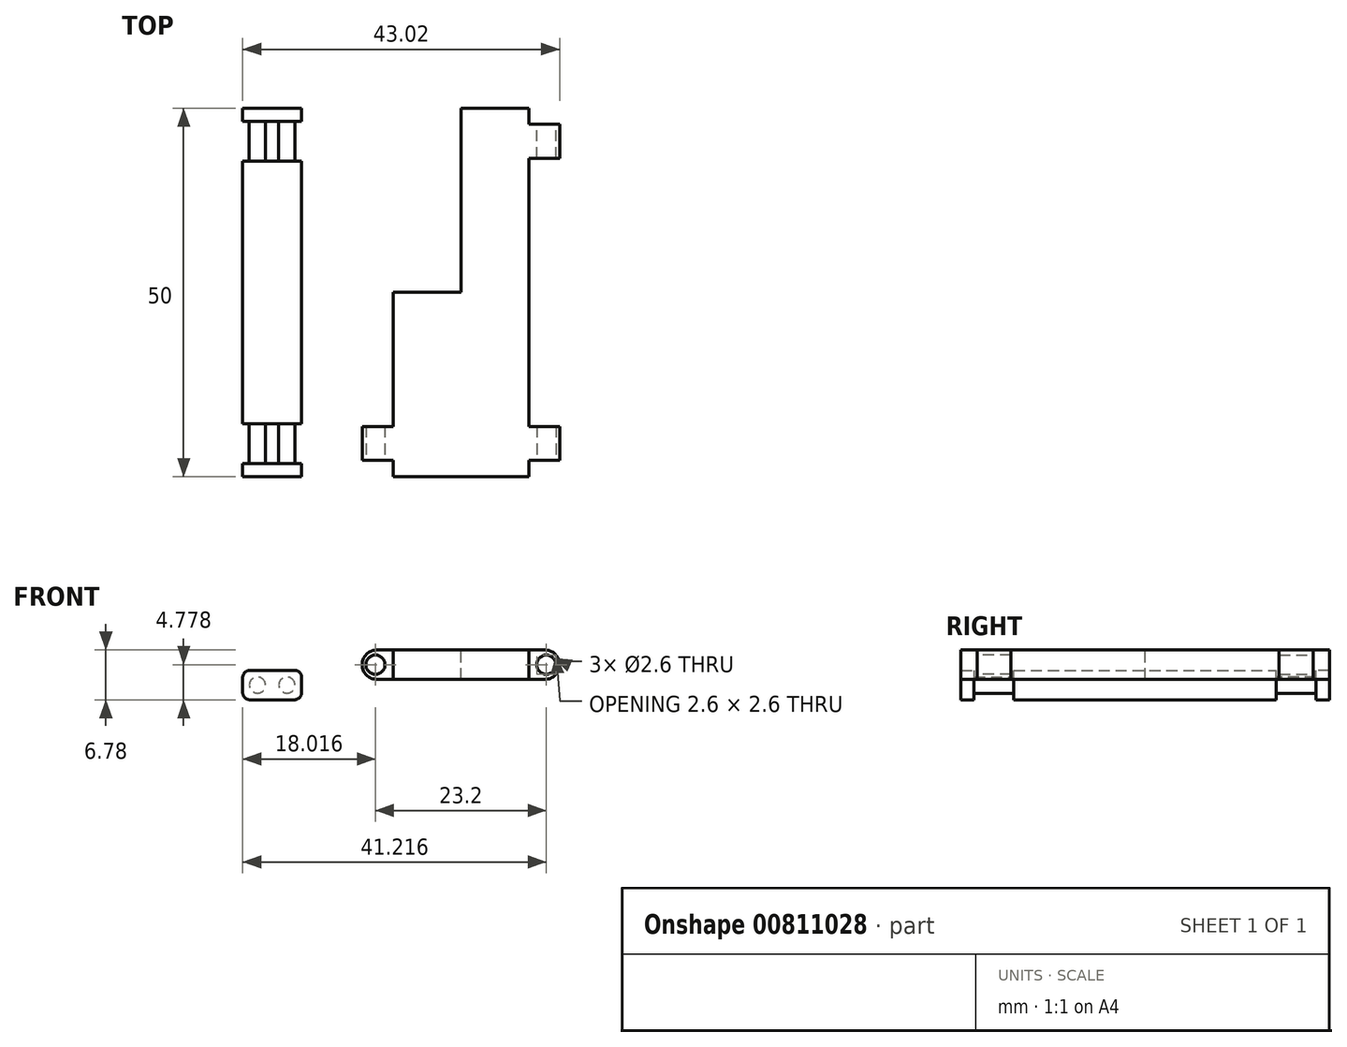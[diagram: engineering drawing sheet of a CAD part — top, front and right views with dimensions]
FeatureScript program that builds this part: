
annotation { "Feature Type Name" : "Feature", "Feature Type Description" : "" }
export const myFeature = defineFeature(function(context is Context, id is Id, definition is map)
    precondition{}
    {
        {
            var Q0;
            Q0=qCreatedBy(makeId("Front.planeOp"),FACE);
            var sketch = newSketch(context, id + "F0", { "sketchPlane" : qUnion([Q0])});
            skLineSegment(sketch, "E0.bottom", {"start": v(-56.99, 28.8) * mm, "end": v(-48.99, 28.8) * mm});
            skLineSegment(sketch, "E0.top", {"start": v(-56.99, 24.8) * mm, "end": v(-48.99, 24.8) * mm});
            skLineSegment(sketch, "E0.left", {"start": v(-56.99, 28.8) * mm, "end": v(-56.99, 24.8) * mm});
            skLineSegment(sketch, "E0.right", {"start": v(-48.99, 28.8) * mm, "end": v(-48.99, 24.8) * mm});
            skSolve(sketch);
        }
        {
            var Q0;
            Q0 = qSketchRegion(id + "F0", true);
            extrude(context, id + "F1", {"entities" : qUnion([Q0]), "depth" : 25 * mm, "offsetDistance" : 25 * mm});
        }
        {
            var Q0;
            Q0=makeQuery(id+"F1.opExtrude","SWEPT_FACE",FACE,{"disambiguationData":[OSD([sQuery(id+"F0.wireOp",EDGE,"E0.bottom")])]});
            var sketch = newSketch(context, id + "F2", { "sketchPlane" : qUnion([Q0])});
            skLineSegment(sketch, "E1.bottom", {"start": v(-56.99, -23.2) * mm, "end": v(-48.99, -23.2) * mm});
            skLineSegment(sketch, "E1.top", {"start": v(-56.99, -17.8) * mm, "end": v(-48.99, -17.8) * mm});
            skLineSegment(sketch, "E1.left", {"start": v(-56.99, -23.2) * mm, "end": v(-56.99, -17.8) * mm});
            skLineSegment(sketch, "E1.right", {"start": v(-48.99, -23.2) * mm, "end": v(-48.99, -17.8) * mm});
            skSolve(sketch);
        }
        {
            var Q0;
            Q0 = qSketchRegion(id + "F2", true);
            extrude(context, id + "F3", {"entities" : qUnion([Q0]), "operationType" : NewBodyOperationType.REMOVE, "oppositeDirection" : true, "depth" : 25 * mm, "offsetDistance" : 25 * mm});
        }
        {
            var Q0;
            Q0=makeQuery(id+"F3.boolean.opBoolean","COPY",FACE,{"derivedFrom":makeQuery(id+"F3.opExtrude","SWEPT_FACE",FACE,{"disambiguationData":[OSD([sQuery(id+"F2.wireOp",EDGE,"E1.top")])]})});
            var sketch = newSketch(context, id + "F4", { "sketchPlane" : qUnion([Q0])});
            skCircle(sketch, "E2", {"center": v(-54.99, 26.8) * mm, "radius": 1.1 * mm});
            skCircle(sketch, "E3", {"center": v(-50.99, 26.8) * mm, "radius": 1.1 * mm});
            skLineSegment(sketch, "E4", {"start": v(-56.99, 26.8) * mm, "end": v(-48.99, 26.8) * mm, "construction": true});
            skSolve(sketch);
        }
        {
            var Q0;
            Q0 = qSketchRegion(id + "F4", true);
            extrude(context, id + "F5", {"entities" : qUnion([Q0]), "operationType" : NewBodyOperationType.ADD, "depth" : 7 * mm, "offsetDistance" : 25 * mm});
        }
        {
            var Q0;
            {var subQ0=sQuery(id+"F0.wireOp",EDGE,"E0.bottom");var subQ1=sQuery(id+"F0.wireOp",EDGE,"E0.left");Q0=makeQuery(id+"F3.boolean.opBoolean","SPLIT",EDGE,{"disambiguationData":[TD([makeQuery(id+"F3.opExtrude","SWEPT_FACE",FACE,{"disambiguationData":[OSD([sQuery(id+"F2.wireOp",EDGE,"E1.top")])]})])],"derivedFrom":makeQuery(id+"F1.opExtrude","SWEPT_EDGE",EDGE,{"disambiguationData":[OSD([subQ0,subQ1])]})});}
            var Q1;
            {var subQ0=sQuery(id+"F0.wireOp",EDGE,"E0.bottom");var subQ1=sQuery(id+"F0.wireOp",EDGE,"E0.right");Q1=makeQuery(id+"F3.boolean.opBoolean","SPLIT",EDGE,{"disambiguationData":[TD([makeQuery(id+"F3.opExtrude","SWEPT_FACE",FACE,{"disambiguationData":[OSD([sQuery(id+"F2.wireOp",EDGE,"E1.top")])]})])],"derivedFrom":makeQuery(id+"F1.opExtrude","SWEPT_EDGE",EDGE,{"disambiguationData":[OSD([subQ0,subQ1])]})});}
            var Q2;
            {var subQ0=sQuery(id+"F0.wireOp",EDGE,"E0.right");var subQ1=sQuery(id+"F0.wireOp",EDGE,"E0.top");Q2=makeQuery(id+"F3.boolean.opBoolean","SPLIT",EDGE,{"disambiguationData":[TD([makeQuery(id+"F3.opExtrude","SWEPT_FACE",FACE,{"disambiguationData":[OSD([sQuery(id+"F2.wireOp",EDGE,"E1.top")])]})])],"derivedFrom":makeQuery(id+"F1.opExtrude","SWEPT_EDGE",EDGE,{"disambiguationData":[OSD([subQ1,subQ0])]})});}
            var Q3;
            {var subQ0=sQuery(id+"F0.wireOp",EDGE,"E0.bottom");var subQ1=sQuery(id+"F0.wireOp",EDGE,"E0.right");Q3=makeQuery(id+"F3.boolean.opBoolean","SPLIT",EDGE,{"disambiguationData":[TD([makeQuery(id+"F3.opExtrude","SWEPT_FACE",FACE,{"disambiguationData":[OSD([sQuery(id+"F2.wireOp",EDGE,"E1.bottom")])]})])],"derivedFrom":makeQuery(id+"F1.opExtrude","SWEPT_EDGE",EDGE,{"disambiguationData":[OSD([subQ0,subQ1])]})});}
            var Q4;
            {var subQ0=sQuery(id+"F0.wireOp",EDGE,"E0.bottom");var subQ1=sQuery(id+"F0.wireOp",EDGE,"E0.left");Q4=makeQuery(id+"F3.boolean.opBoolean","SPLIT",EDGE,{"disambiguationData":[TD([makeQuery(id+"F3.opExtrude","SWEPT_FACE",FACE,{"disambiguationData":[OSD([sQuery(id+"F2.wireOp",EDGE,"E1.bottom")])]})])],"derivedFrom":makeQuery(id+"F1.opExtrude","SWEPT_EDGE",EDGE,{"disambiguationData":[OSD([subQ0,subQ1])]})});}
            var Q5;
            {var subQ0=sQuery(id+"F0.wireOp",EDGE,"E0.right");var subQ1=sQuery(id+"F0.wireOp",EDGE,"E0.top");Q5=makeQuery(id+"F3.boolean.opBoolean","SPLIT",EDGE,{"disambiguationData":[TD([makeQuery(id+"F3.opExtrude","SWEPT_FACE",FACE,{"disambiguationData":[OSD([sQuery(id+"F2.wireOp",EDGE,"E1.bottom")])]})])],"derivedFrom":makeQuery(id+"F1.opExtrude","SWEPT_EDGE",EDGE,{"disambiguationData":[OSD([subQ1,subQ0])]})});}
            var Q6;
            {var subQ0=sQuery(id+"F0.wireOp",EDGE,"E0.left");var subQ1=sQuery(id+"F0.wireOp",EDGE,"E0.top");Q6=makeQuery(id+"F3.boolean.opBoolean","SPLIT",EDGE,{"disambiguationData":[TD([makeQuery(id+"F3.opExtrude","SWEPT_FACE",FACE,{"disambiguationData":[OSD([sQuery(id+"F2.wireOp",EDGE,"E1.top")])]})])],"derivedFrom":makeQuery(id+"F1.opExtrude","SWEPT_EDGE",EDGE,{"disambiguationData":[OSD([subQ1,subQ0])]})});}
            var Q7;
            {var subQ0=sQuery(id+"F0.wireOp",EDGE,"E0.left");var subQ1=sQuery(id+"F0.wireOp",EDGE,"E0.top");Q7=makeQuery(id+"F3.boolean.opBoolean","SPLIT",EDGE,{"disambiguationData":[TD([makeQuery(id+"F3.opExtrude","SWEPT_FACE",FACE,{"disambiguationData":[OSD([sQuery(id+"F2.wireOp",EDGE,"E1.bottom")])]})])],"derivedFrom":makeQuery(id+"F1.opExtrude","SWEPT_EDGE",EDGE,{"disambiguationData":[OSD([subQ1,subQ0])]})});}
            fillet(context, id + "F6", {"entities" : qUnion([Q0, Q1, Q2, Q3, Q4, Q5, Q6, Q7]), "radius" : 1 * mm, "tangentPropagation" : true, "allowEdgeOverflow" : false});
        }
        {
            var Q0;
            Q0=makeQuery(id+"F3.boolean.opBoolean","SPLIT",BODY,{"disambiguationData":[OD(0.0)],"derivedFrom":makeQuery(id+"F1.opExtrude","SWEPT_BODY",BODY,{"disambiguationData":[OSD([sQuery(id+"F0.wireOp",EDGE,"E0.bottom"),sQuery(id+"F0.wireOp",EDGE,"E0.top"),sQuery(id+"F0.wireOp",EDGE,"E0.left"),sQuery(id+"F0.wireOp",EDGE,"E0.right")])]})});
            var Q1;
            Q1=qCreatedBy(makeId("Front.planeOp"),FACE);
            mirror(context, id + "F7", {"operationType" : NewBodyOperationType.ADD, "entities" : qUnion([Q0]), "mirrorPlane" : qUnion([Q1])});
        }
        {
            var Q0;
            Q0=qCreatedBy(makeId("Front.planeOp"),FACE);
            var sketch = newSketch(context, id + "F8", { "sketchPlane" : qUnion([Q0])});
            skLineSegment(sketch, "E5.bottom", {"start": v(-27.37, 27.57) * mm, "end": v(-18.17, 27.57) * mm});
            skLineSegment(sketch, "E5.top", {"start": v(-27.37, 31.57) * mm, "end": v(-18.17, 31.57) * mm});
            skLineSegment(sketch, "E5.left", {"start": v(-27.37, 27.57) * mm, "end": v(-27.37, 31.57) * mm});
            skLineSegment(sketch, "E5.right", {"start": v(-18.17, 27.57) * mm, "end": v(-18.17, 31.57) * mm});
            skSolve(sketch);
        }
        {
            var Q0;
            Q0 = qSketchRegion(id + "F8", true);
            extrude(context, id + "F9", {"entities" : qUnion([Q0]), "depth" : 25 * mm, "offsetDistance" : 25 * mm});
        }
        {
            var Q0;
            Q0=makeQuery(id+"F9.opExtrude","SWEPT_FACE",FACE,{"disambiguationData":[OSD([sQuery(id+"F8.wireOp",EDGE,"E5.right")])]});
            var sketch = newSketch(context, id + "F10", { "sketchPlane" : qUnion([Q0])});
            skLineSegment(sketch, "E6", {"start": v(-23, 31.57) * mm, "end": v(-23, 27.57) * mm, "construction": true});
            skLineSegment(sketch, "E7", {"start": v(-18, 31.57) * mm, "end": v(-18, 27.57) * mm, "construction": true});
            skLineSegment(sketch, "E8.bottom", {"start": v(-22.8, 31.57) * mm, "end": v(-18.2, 31.57) * mm});
            skLineSegment(sketch, "E8.top", {"start": v(-22.8, 27.57) * mm, "end": v(-18.2, 27.57) * mm});
            skLineSegment(sketch, "E8.left", {"start": v(-22.8, 31.57) * mm, "end": v(-22.8, 27.57) * mm});
            skLineSegment(sketch, "E8.right", {"start": v(-18.2, 31.57) * mm, "end": v(-18.2, 27.57) * mm});
            skSolve(sketch);
        }
        {
            var Q0;
            Q0 = qSketchRegion(id + "F10", true);
            extrude(context, id + "F11", {"entities" : qUnion([Q0]), "operationType" : NewBodyOperationType.ADD, "depth" : 4.2 * mm, "offsetDistance" : 25 * mm});
        }
        {
            var Q0;
            Q0=makeQuery(id+"F11.opExtrude","SWEPT_FACE",FACE,{"disambiguationData":[OSD([sQuery(id+"F10.wireOp",EDGE,"E8.left")])]});
            var sketch = newSketch(context, id + "F12", { "sketchPlane" : qUnion([Q0])});
            skLineSegment(sketch, "E9", {"start": v(-18.17, 29.57) * mm, "end": v(-13.97, 29.57) * mm, "construction": true});
            skCircle(sketch, "E10", {"center": v(-15.77, 29.57) * mm, "radius": 1.3 * mm});
            skSolve(sketch);
        }
        {
            var Q0;
            Q0 = qSketchRegion(id + "F12", true);
            extrude(context, id + "F13", {"entities" : qUnion([Q0]), "operationType" : NewBodyOperationType.REMOVE, "oppositeDirection" : true, "depth" : 25 * mm, "offsetDistance" : 25 * mm});
        }
        {
            var Q0;
            Q0=makeQuery(id+"F11.opExtrude","CAP_EDGE",EDGE,{"disambiguationData":[OSD([sQuery(id+"F10.wireOp",EDGE,"E8.bottom")])],"isStart":false});
            var Q1;
            Q1=makeQuery(id+"F11.opExtrude","CAP_EDGE",EDGE,{"disambiguationData":[OSD([sQuery(id+"F10.wireOp",EDGE,"E8.top")])],"isStart":false});
            fillet(context, id + "F14", {"entities" : qUnion([Q0, Q1]), "radius" : 2 * mm, "tangentPropagation" : true, "allowEdgeOverflow" : false});
        }
        {
            var Q0;
            Q0=makeQuery(id+"F9.opExtrude","SWEPT_BODY",BODY,{"disambiguationData":[OSD([sQuery(id+"F8.wireOp",EDGE,"E5.bottom"),sQuery(id+"F8.wireOp",EDGE,"E5.top"),sQuery(id+"F8.wireOp",EDGE,"E5.left"),sQuery(id+"F8.wireOp",EDGE,"E5.right")])]});
            var Q1;
            Q1=makeQuery(id+"F9.opExtrude","SWEPT_FACE",FACE,{"disambiguationData":[OSD([sQuery(id+"F8.wireOp",EDGE,"E5.left")])]});
            mirror(context, id + "F15", {"operationType" : NewBodyOperationType.ADD, "entities" : qUnion([Q0]), "mirrorPlane" : qUnion([Q1])});
        }
        {
            var Q0;
            Q0=makeQuery(id+"F9.opExtrude","SWEPT_BODY",BODY,{"disambiguationData":[OSD([sQuery(id+"F8.wireOp",EDGE,"E5.bottom"),sQuery(id+"F8.wireOp",EDGE,"E5.top"),sQuery(id+"F8.wireOp",EDGE,"E5.left"),sQuery(id+"F8.wireOp",EDGE,"E5.right")])]});
            var Q1;
            {var subQ0=makeQuery(id+"F9.opExtrude","CAP_FACE",FACE,{"disambiguationData":[OSD([sQuery(id+"F8.wireOp",EDGE,"E5.bottom"),sQuery(id+"F8.wireOp",EDGE,"E5.top"),sQuery(id+"F8.wireOp",EDGE,"E5.left"),sQuery(id+"F8.wireOp",EDGE,"E5.right")])],"isStart":true});Q1=makeQuery(id+"F15.boolean.opBoolean","MERGE",FACE,{"derivedFrom":[subQ0,makeQuery(id+"F15.opPattern","COPY",FACE,{"derivedFrom":subQ0,"instanceName":"1"})]});}
            mirror(context, id + "F16", {"operationType" : NewBodyOperationType.ADD, "entities" : qUnion([Q0]), "mirrorPlane" : qUnion([Q1])});
        }
    });
